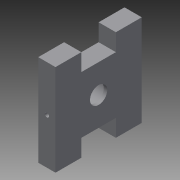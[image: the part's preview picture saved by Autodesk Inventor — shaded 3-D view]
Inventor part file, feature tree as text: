
AUTODESK INVENTOR PART (.ipt)
format: ipt  version: 2015 (Build 190159000, 159)  size: 118,784 bytes
history: native  units: mm
features: sketch x6, extrude x4, fillet x1
ambient origin geometry x8: Origin, YZ Plane, XZ Plane, XY Plane, X Axis, Y Axis, Z Axis, Center Point
bodies: Solid1 (feature_tree)
feature tree (11):
  sketch  "Sketch1"  dims[d0=50.0mm d1=53.0mm]
  sketch  "Sketch2"  dims[d2=15.0mm d3=10.0mm]
  extrude  "Extrusion1"  Depth=53.0mm
  sketch  "Sketch4"  dims[d6=15.0mm d7=10.0mm d8=20.0mm]
  sketch  "Sketch5"  dims[d9=10.0mm]
  sketch  "Sketch6"  dims[d10=15.0mm d11=10.0mm d12=0.0mm d13=15.0mm d28=10.0mm d29=0.0mm d30=2.5mm d31=10.0mm d32=0.0mm d33=10.0mm d34=2.0mm d35=0.0mm d36=2.0mm]
  extrude  "Extrusion2"  Depth=10.0mm
  extrude  "Extrusion3"  Depth=10.0mm
  extrude  "Extrusion4"  Depth=10.0mm
  fillet  "Fillet1"  Radius=20.0mm
  sketch  "Sketch3"  dims[d4=20.0mm d5=10.0mm]
